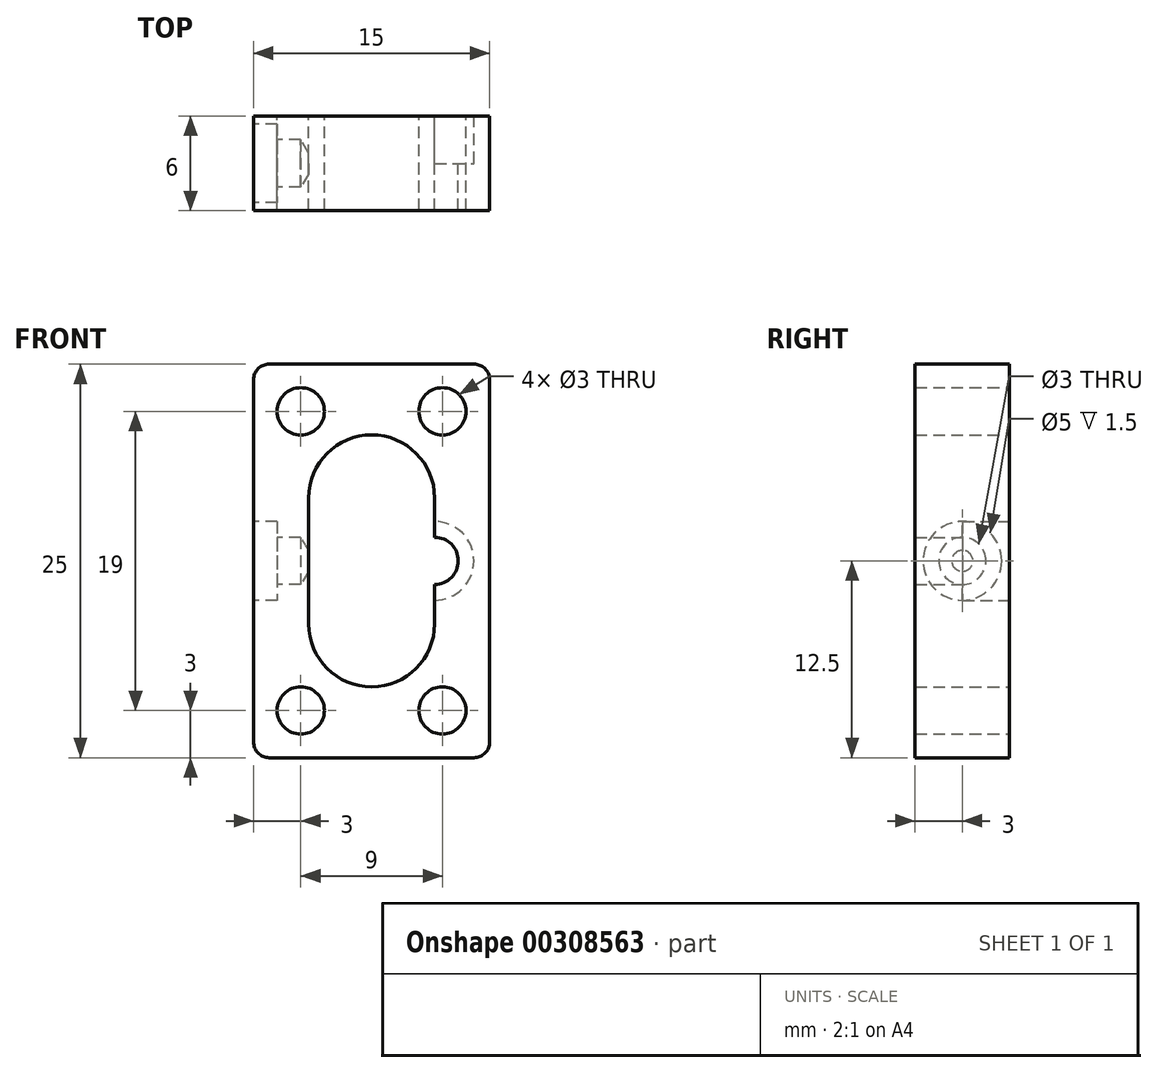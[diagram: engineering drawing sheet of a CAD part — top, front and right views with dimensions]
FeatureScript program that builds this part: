
annotation { "Feature Type Name" : "Feature", "Feature Type Description" : "" }
export const myFeature = defineFeature(function(context is Context, id is Id, definition is map)
    precondition{}
    {
        {
            var Q0;
            Q0=qCreatedBy(makeId("Front.planeOp"),FACE);
            var sketch = newSketch(context, id + "F0", { "sketchPlane" : qUnion([Q0])});
            skLineSegment(sketch, "E0.bottom", {"start": v(7.5, -12.5) * mm, "end": v(-7.5, -12.5) * mm});
            skLineSegment(sketch, "E0.top", {"start": v(7.5, 12.5) * mm, "end": v(-7.5, 12.5) * mm});
            skLineSegment(sketch, "E0.left", {"start": v(7.5, -12.5) * mm, "end": v(7.5, 12.5) * mm});
            skLineSegment(sketch, "E0.right", {"start": v(-7.5, -12.5) * mm, "end": v(-7.5, 12.5) * mm});
            skPoint(sketch, "E0.middle", {"position": v(0, 0) * mm});
            skPoint(sketch, "E1.endSnap0", {"position": v(0, -12.5) * mm});
            skLineSegment(sketch, "E2", {"start": v(0, 0) * mm, "end": v(0, 9.5) * mm, "construction": true});
            skLineSegment(sketch, "E3", {"start": v(0, 9.5) * mm, "end": v(-4.5, 9.5) * mm, "construction": true});
            skLineSegment(sketch, "E4", {"start": v(0, 0) * mm, "end": v(0, -9.5) * mm, "construction": true});
            skLineSegment(sketch, "E5", {"start": v(0, -9.5) * mm, "end": v(-4.5, -9.5) * mm, "construction": true});
            skCircle(sketch, "E6", {"center": v(-4.5, 9.5) * mm, "radius": 1.5 * mm});
            skCircle(sketch, "E7", {"center": v(-4.5, -9.5) * mm, "radius": 1.5 * mm});
            skCircle(sketch, "E8.MirrorC", {"center": v(4.5, 9.5) * mm, "radius": 1.5 * mm});
            skCircle(sketch, "E9.MirrorC", {"center": v(4.5, -9.5) * mm, "radius": 1.5 * mm});
            skLineSegment(sketch, "E10", {"start": v(0, 4) * mm, "end": v(0, -4) * mm, "construction": true});
            skArc(sketch, "E11.0.startCap", {"start": v(-4, 4) * mm, "mid": v(0, 8) * mm, "end": v(4, 4) * mm});
            skArc(sketch, "E11.0.endCap", {"start": v(4, -4) * mm, "mid": v(0, -8) * mm, "end": v(-4, -4) * mm});
            skLineSegment(sketch, "E11.0.left", {"start": v(4, 4) * mm, "end": v(4, 1.5) * mm});
            skLineSegment(sketch, "E11.0.right", {"start": v(-4, 4) * mm, "end": v(-4, -4) * mm});
            skArc(sketch, "E12", {"start": v(4, -1.5) * mm, "mid": v(5.5, 0) * mm, "end": v(4, 1.5) * mm});
            skCircle(sketch, "E13", {"center": v(0, -4) * mm, "radius": 2 * mm});
            skLineSegment(sketch, "E14.trimOffspring", {"start": v(4, -1.5) * mm, "end": v(4, -4) * mm});
            skSolve(sketch);
        }
        {
            var Q0;
            Q0=makeQuery(id+"F0.imprint","IMPRINT",FACE,{"disambiguationData":[TD([[makeQuery(id+"F0.imprint","IMPRINT",EDGE,{"derivedFrom":sQuery(id+"F0.wireOp",EDGE,"E0.bottom")}),-1.0]])]});
            extrude(context, id + "F1", {"entities" : qUnion([Q0]), "endBound" : BoundingType.SYMMETRIC, "depth" : 6 * mm});
        }
        {
            var Q0;
            Q0=makeQuery(id+"F0.imprint","IMPRINT",FACE,{"disambiguationData":[TD([[makeQuery(id+"F0.imprint","IMPRINT",EDGE,{"derivedFrom":sQuery(id+"F0.wireOp",EDGE,"E11.0.startCap")}),-1.0]])]});
            extrude(context, id + "F2", {"entities" : qUnion([Q0]), "operationType" : NewBodyOperationType.ADD, "oppositeDirection" : true, "depth" : 3 * mm});
        }
        {
            var Q0;
            {var subQ0=sQuery(id+"F0.wireOp",EDGE,"E14.trimOffspring");var subQ1=sQuery(id+"F0.wireOp",EDGE,"E12");var subQ2=sQuery(id+"F0.wireOp",EDGE,"E11.0.right");var subQ3=sQuery(id+"F0.wireOp",EDGE,"E11.0.left");var subQ4=sQuery(id+"F0.wireOp",EDGE,"E11.0.endCap");var subQ5=sQuery(id+"F0.wireOp",EDGE,"E11.0.startCap");Q0=makeQuery(id+"F2.boolean.opBoolean","MERGE",FACE,{"derivedFrom":[makeQuery(id+"F1.opExtrude","CAP_FACE",FACE,{"disambiguationData":[OSD([sQuery(id+"F0.wireOp",EDGE,"E0.bottom"),sQuery(id+"F0.wireOp",EDGE,"E0.top"),sQuery(id+"F0.wireOp",EDGE,"E0.left"),sQuery(id+"F0.wireOp",EDGE,"E0.right"),sQuery(id+"F0.wireOp",EDGE,"E6"),sQuery(id+"F0.wireOp",EDGE,"E7"),sQuery(id+"F0.wireOp",EDGE,"E8.MirrorC"),sQuery(id+"F0.wireOp",EDGE,"E9.MirrorC"),subQ5,subQ4,subQ3,subQ2,subQ1,subQ0])],"isStart":true}),makeQuery(id+"F2.opExtrude","CAP_FACE",FACE,{"disambiguationData":[OSD([subQ5,subQ4,subQ3,subQ2,subQ1,sQuery(id+"F0.wireOp",EDGE,"E13"),subQ0])],"isStart":false})]});}
            var sketch = newSketch(context, id + "F3", { "sketchPlane" : qUnion([Q0])});
            skPoint(sketch, "E15.0", {"position": v(-4, 0) * mm});
            skCircle(sketch, "E16", {"center": v(-4, 0) * mm, "radius": 2.5 * mm});
            skSolve(sketch);
        }
        {
            var Q0;
            Q0 = qSketchRegion(id + "F3", true);
            extrude(context, id + "F4", {"entities" : qUnion([Q0]), "operationType" : NewBodyOperationType.REMOVE, "oppositeDirection" : true, "depth" : 3 * mm});
        }
        {
            var Q0;
            Q0=makeQuery(id+"F1.opExtrude","SWEPT_FACE",FACE,{"disambiguationData":[OSD([sQuery(id+"F0.wireOp",EDGE,"E0.right")])]});
            var sketch = newSketch(context, id + "F5", { "sketchPlane" : qUnion([Q0])});
            skCircle(sketch, "E17", {"center": v(0, 0) * mm, "radius": 2.5 * mm});
            skCircle(sketch, "E18", {"center": v(0, 0) * mm, "radius": 1.5 * mm});
            skSolve(sketch);
        }
        {
            var Q0;
            Q0=sQuery(id+"F5.wireOp",VERTEX,"E17.center");
            var Q1;
            Q1=makeQuery(id+"F1.opExtrude","SWEPT_BODY",BODY,{"disambiguationData":[OSD([sQuery(id+"F0.wireOp",EDGE,"E0.bottom"),sQuery(id+"F0.wireOp",EDGE,"E0.top"),sQuery(id+"F0.wireOp",EDGE,"E0.left"),sQuery(id+"F0.wireOp",EDGE,"E0.right"),sQuery(id+"F0.wireOp",EDGE,"E6"),sQuery(id+"F0.wireOp",EDGE,"E7"),sQuery(id+"F0.wireOp",EDGE,"E8.MirrorC"),sQuery(id+"F0.wireOp",EDGE,"E9.MirrorC"),sQuery(id+"F0.wireOp",EDGE,"E11.0.startCap"),sQuery(id+"F0.wireOp",EDGE,"E11.0.endCap"),sQuery(id+"F0.wireOp",EDGE,"E11.0.left"),sQuery(id+"F0.wireOp",EDGE,"E11.0.right"),sQuery(id+"F0.wireOp",EDGE,"E12"),sQuery(id+"F0.wireOp",EDGE,"E14.trimOffspring")])]});
            hole(context, id + "F6", {"style" : HoleStyle.C_BORE, "endStyle" : HoleEndStyle.BLIND, "holeDiameter" : 3 * mm, "cBoreDiameter" : 5 * mm, "cBoreDepth" : 1.5 * mm, "holeDepth" : 3 * mm, "tappedDepth" : 12 * mm, "tapClearance" : 3, "locations" : qUnion([Q0]), "scope" : qUnion([Q1])});
        }
        {
            var Q0;
            Q0=makeQuery(id+"F1.opExtrude","SWEPT_EDGE",EDGE,{"disambiguationData":[OSD([sQuery(id+"F0.wireOp",EDGE,"E0.bottom"),sQuery(id+"F0.wireOp",EDGE,"E0.left")])]});
            var Q1;
            Q1=makeQuery(id+"F1.opExtrude","SWEPT_EDGE",EDGE,{"disambiguationData":[OSD([sQuery(id+"F0.wireOp",EDGE,"E0.bottom"),sQuery(id+"F0.wireOp",EDGE,"E0.right")])]});
            var Q2;
            Q2=makeQuery(id+"F1.opExtrude","SWEPT_EDGE",EDGE,{"disambiguationData":[OSD([sQuery(id+"F0.wireOp",EDGE,"E0.top"),sQuery(id+"F0.wireOp",EDGE,"E0.right")])]});
            var Q3;
            Q3=makeQuery(id+"F1.opExtrude","SWEPT_EDGE",EDGE,{"disambiguationData":[OSD([sQuery(id+"F0.wireOp",EDGE,"E0.top"),sQuery(id+"F0.wireOp",EDGE,"E0.left")])]});
            fillet(context, id + "F7", {"entities" : qUnion([Q0, Q1, Q2, Q3]), "radius" : 1 * mm, "tangentPropagation" : true, "allowEdgeOverflow" : false});
        }
    });
